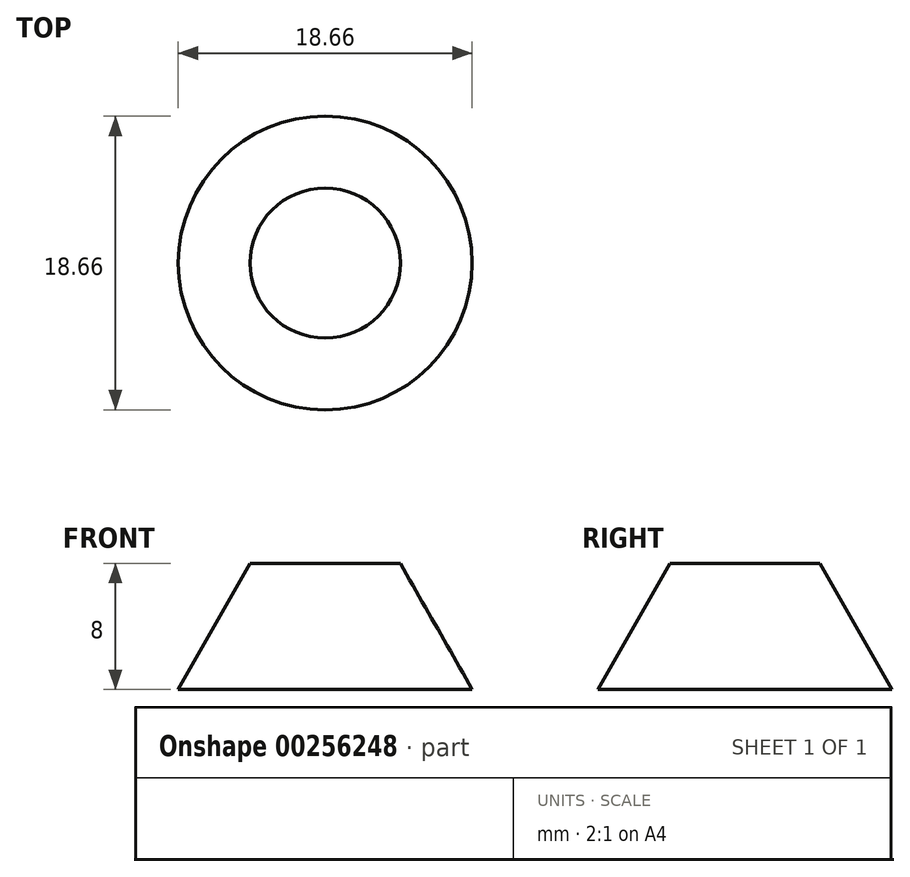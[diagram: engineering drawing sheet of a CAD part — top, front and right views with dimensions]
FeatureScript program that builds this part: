
annotation { "Feature Type Name" : "Feature", "Feature Type Description" : "" }
export const myFeature = defineFeature(function(context is Context, id is Id, definition is map)
    precondition{}
    {
        {
            var Q0;
            Q0=qCreatedBy(makeId("Front.planeOp"),FACE);
            var sketch = newSketch(context, id + "F0", { "sketchPlane" : qUnion([Q0])});
            skLineSegment(sketch, "E0", {"start": v(0, 0) * mm, "end": v(0, 8) * mm});
            skLineSegment(sketch, "E1", {"start": v(0, 8) * mm, "end": v(4.77, 8) * mm});
            skLineSegment(sketch, "E2", {"start": v(4.77, 8) * mm, "end": v(9.33, 0) * mm});
            skLineSegment(sketch, "E3", {"start": v(9.33, 0) * mm, "end": v(0, 0) * mm});
            skLineSegment(sketch, "E4", {"start": v(0, 9.9) * mm, "end": v(0, -5.08) * mm, "construction": true});
            skSolve(sketch);
        }
        {
            var Q0;
            Q0=makeQuery(id+"F0.imprint","IMPRINT",FACE,{"disambiguationData":[TD([[makeQuery(id+"F0.imprint","IMPRINT",EDGE,{"derivedFrom":sQuery(id+"F0.wireOp",EDGE,"E0")}),-1.0]])]});
            var Q1;
            Q1=sQuery(id+"F0.wireOp",EDGE,"E4");
            revolve(context, id + "F1", {"entities" : qUnion([Q0]), "axis" : qUnion([Q1]), "revolveType" : RevolveType.FULL});
        }
    });
